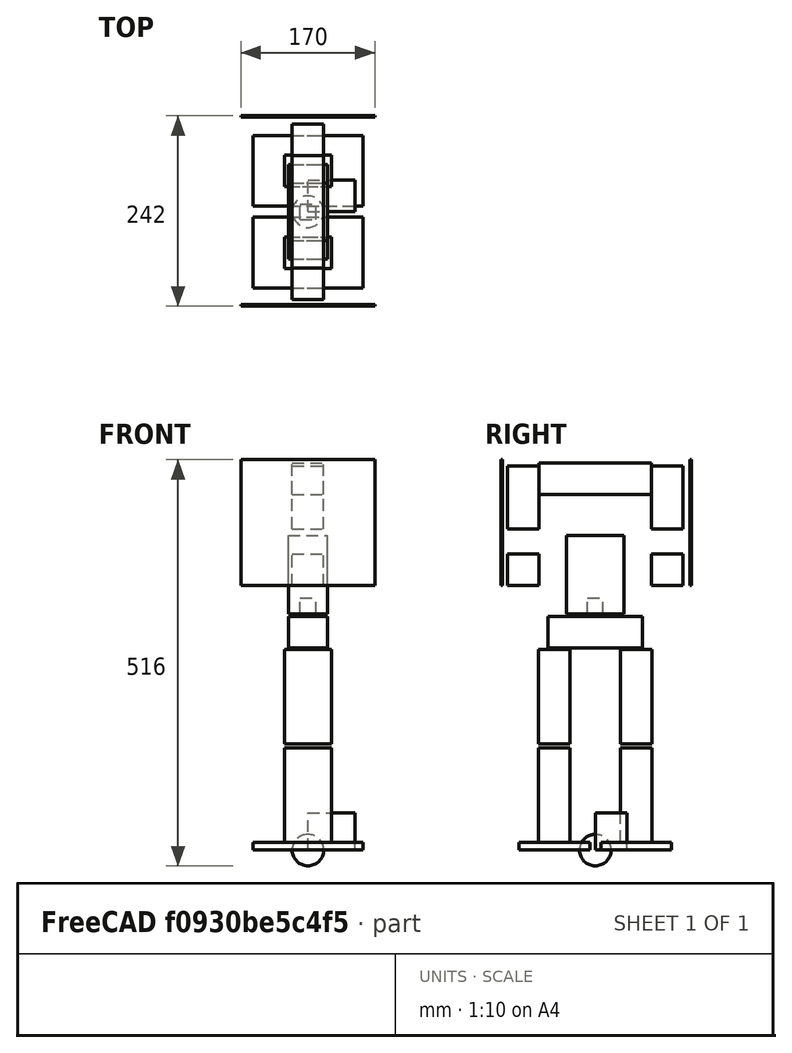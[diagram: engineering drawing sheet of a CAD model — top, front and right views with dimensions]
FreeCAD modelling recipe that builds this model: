
FCSTD DOCUMENT  (FreeCAD 1.1R20260414 (Git shallow))
Label: mj_urdf
License: All rights reserved
LicenseURL: https://en.wikipedia.org/wiki/All_rights_reserved
objects: App::FeaturePython×47, App::Link×43, App::Point×21, App::Part×21, Part::Box×18, Part::Sphere×4, App::DocumentObjectGroup×2, App::DocumentObjectGroupPython×1
note: 22 computed .brp shape members not serialized (recipe doc carries the construction recipe); baked Part::Feature solids carry a one-line shape summary decoded from their .brp

FEATURE [Part::Box] Box001  label="waist_body001"
  AttacherType = Attacher::AttachEngine3D
  Height = 40
  Length = 50
  Placement = pos=(-25,-60,257) rot=(0,0,1;0rad)
  Width = 120
  expr: .Placement.Base.x = -Length / 2
  expr: .Placement.Base.y = -Width / 2
FEATURE [Part::Box] Box002  label="right_thigh"
  AttacherType = Attacher::AttachEngine3D
  Height = 120
  Length = 60
  Placement = pos=(-30,-72,135) rot=(0,0,1;0rad)
  Width = 40
  expr: .Placement.Base.x = -Length / 2
  expr: .Placement.Base.y = -104 mm / 2 - Width / 2
FEATURE [Part::Box] Box003  label="right_shin"
  AttacherType = Attacher::AttachEngine3D
  Height = 120
  Length = 60
  Placement = pos=(-30,-72,10) rot=(0,0,1;0rad)
  Width = 40
  expr: .Placement.Base.x = -Length / 2
  expr: .Placement.Base.y = -104 mm / 2 - Width / 2
FEATURE [Part::Box] Box004  label="right_sole"
  AttacherType = Attacher::AttachEngine3D
  Height = 10
  Length = 140
  Placement = pos=(-70,-97,0) rot=(0,0,1;0rad)
  Width = 90
  expr: .Placement.Base.x = -Length / 2
  expr: .Placement.Base.y = -104 mm / 2 - Width / 2
FEATURE [Part::Box] Box005  label="left_thigh"
  AttacherType = Attacher::AttachEngine3D
  Height = 120
  Length = 60
  Placement = pos=(-30,32,135) rot=(0,0,1;0rad)
  Width = 40
  expr: .Placement.Base.x = -Length / 2
  expr: .Placement.Base.y = +104 mm / 2 - Width / 2
FEATURE [Part::Box] Box006  label="left_shin"
  AttacherType = Attacher::AttachEngine3D
  Height = 120
  Length = 60
  Placement = pos=(-30,32,10) rot=(0,0,1;0rad)
  Width = 40
  expr: .Placement.Base.x = -Length / 2
  expr: .Placement.Base.y = +104 mm / 2 - Width / 2
FEATURE [Part::Box] Box007  label="left_sole"
  AttacherType = Attacher::AttachEngine3D
  Height = 10
  Length = 140
  Placement = pos=(-70,7,0) rot=(0,0,1;0rad)
  Width = 90
  expr: .Placement.Base.x = -Length / 2
  expr: .Placement.Base.y = +104 mm / 2 - Width / 2
FEATURE [Part::Box] Box008  label="body_sholder"
  AttacherType = Attacher::AttachEngine3D
  Height = 40
  Length = 40
  Placement = pos=(-20,-71.5,452) rot=(0,0,1;0rad)
  Width = 143
  expr: .Placement.Base.x = -Length / 2
  expr: .Placement.Base.y = -Width / 2
FEATURE [Part::Box] Box009  label="right_arm"
  AttacherType = Attacher::AttachEngine3D
  Height = 80
  Length = 40
  Placement = pos=(-20,-111.5,408) rot=(0,0,1;0rad)
  Width = 40
  expr: .Placement.Base.x = -Length / 2
  expr: .Placement.Base.y = -143 mm / 2 - Width
FEATURE [Part::Box] Box010  label="right_wrist"
  AttacherType = Attacher::AttachEngine3D
  Height = 40
  Length = 40
  Placement = pos=(-20,-111.5,336) rot=(0,0,1;0rad)
  Width = 40
  expr: .Placement.Base.x = -Length / 2
  expr: .Placement.Base.y = -143 mm / 2 - Width
FEATURE [Part::Box] Box011  label="right_hand"
  AttacherType = Attacher::AttachEngine3D
  Height = 160
  Length = 170
  Placement = pos=(-85,-120,336) rot=(0,0,1;0rad)
  Width = 2
  expr: .Placement.Base.x = -Length / 2
FEATURE [Part::Box] Box012  label="left_arm"
  AttacherType = Attacher::AttachEngine3D
  Height = 80
  Length = 40
  Placement = pos=(-20,71.5,408) rot=(0,0,1;0rad)
  Width = 40
  expr: .Placement.Base.x = -Length / 2
  expr: .Placement.Base.y = +143 mm / 2
FEATURE [Part::Box] Box014  label="left_hand"
  AttacherType = Attacher::AttachEngine3D
  Height = 160
  Length = 170
  Placement = pos=(-85,120,336) rot=(0,0,1;0rad)
  Width = 2
  expr: .Placement.Base.x = -Length / 2
FEATURE [Part::Box] Box  label="body_parts"
  AttacherType = Attacher::AttachEngine3D
  Height = 100
  Length = 50
  Placement = pos=(-25,-36.5,300) rot=(0,0,1;0rad)
  Width = 73
  expr: .Placement.Base.x = -Length / 2
  expr: .Placement.Base.y = -Width / 2
FEATURE [Part::Box] Box013  label="left_wrist"
  AttacherType = Attacher::AttachEngine3D
  Height = 40
  Length = 40
  Placement = pos=(-20,71.5,336) rot=(0,0,1;0rad)
  Width = 40
  expr: .Placement.Base.x = -Length / 2
  expr: .Placement.Base.y = +143 mm / 2
FEATURE [App::Point] Origin001
  Role = Origin
FEATURE [App::Link] waist001  label="waist002"
  LinkedObject = -> Box001
FEATURE [App::Part] waist  label="waist001"
  Group = -> [waist001]
  Origin = -> Origin
FEATURE [App::Link] real_l_waist001_
  LinkPlacement = pos=(-25,-60,362) rot=(0,0,1;0rad)
  LinkedObject = -> waist
  Placement = pos=(-25,-60,362) rot=(0,0,1;0rad)
FEATURE [App::FeaturePython] l_waist001  label="waist"  # WARN: FeaturePython — macro-defined, semantics opaque (R4)
  CalculateInertiaBasedOnMass = false
  Group = -> [real_l_waist001_]
  Ixx = 0
  Ixy = 0
  Ixz = 0
  Iyy = 0
  Iyz = 0
  Izz = 0
  Mass = 0
  MaterialNotCalculate = false
  MountedPlacement = pos=(-25,-60,362) rot=(0,0,1;0rad)
  Placement = pos=(-25,-60,362) rot=(0,0,1;0rad)
  Real = -> [waist]
  Visual = -> [waist]
  _Type = Cross::Link
  expr: .MountedPlacement.Base.x = -<<waist_body001>>.Length / 2
  expr: .MountedPlacement.Base.y = -<<waist_body001>>.Width / 2
FEATURE [App::Point] Origin003
  Role = Origin
FEATURE [App::Link] body001  label="body002"
  LinkedObject = -> Box
FEATURE [App::Link] real_l_body001_
  LinkPlacement = pos=(-25,-36.5,404.5) rot=(0,0,1;0rad)
  LinkedObject = -> body
  Placement = pos=(-25,-36.5,404.5) rot=(0,0,1;0rad)
FEATURE [App::Link] body_sholder001  label="body_sholder002"
  LinkPlacement = pos=(5,-35,100.5) rot=(0,0,1;0rad)
  LinkedObject = -> Box008
  Placement = pos=(5,-35,100.5) rot=(0,0,1;0rad)
  expr: .Placement.Base.x = -<<body_sholder>>.Length / 2 + <<body_parts>>.Length / 2
  expr: .Placement.Base.y = -<<body_sholder>>.Width / 2 + <<body_parts>>.Width / 2
  expr: .Placement.Base.z = 42.5 mm + 78 mm - <<body_sholder>>.Height / 2
FEATURE [App::Point] Origin007  label="Origin009"
  Role = Origin
FEATURE [App::Link] right_thigh001  label="right_thigh002"
  LinkedObject = -> Box002
FEATURE [App::Part] right_thigh  label="right_thigh001"
  Group = -> [right_thigh001]
  Origin = -> Origin006
FEATURE [App::Link] real_l_right_thigh001_
  LinkPlacement = pos=(-30,-72,217) rot=(0,0,1;0rad)
  LinkedObject = -> right_thigh
  Placement = pos=(-30,-72,217) rot=(0,0,1;0rad)
FEATURE [App::FeaturePython] l_right_thigh001  label="r_thigh"  # WARN: FeaturePython — macro-defined, semantics opaque (R4)
  CalculateInertiaBasedOnMass = false
  Group = -> [real_l_right_thigh001_]
  Ixx = 0
  Ixy = 0
  Ixz = 0
  Iyy = 0
  Iyz = 0
  Izz = 0
  Mass = 0
  MaterialNotCalculate = false
  MountedPlacement = pos=(-110,30,20) rot=(-0.57735,0.57735,-0.57735;2.0944rad)
  Placement = pos=(-30,-72,217) rot=(0,0,1;0rad)
  Real = -> [right_thigh]
  Visual = -> [right_thigh]
  _Type = Cross::Link
  expr: .MountedPlacement.Base.y = <<right_thigh>>.Length / 2
  expr: .MountedPlacement.Base.z = <<right_thigh>>.Width / 2
FEATURE [App::Point] Origin009  label="Origin011"
  Role = Origin
FEATURE [App::Link] right_shin001  label="right_shin002"
  LinkedObject = -> Box003
FEATURE [App::Part] right_shin  label="right_shin001"
  Group = -> [right_shin001]
  Origin = -> Origin008
FEATURE [App::Link] real_l_right_shin001_
  LinkPlacement = pos=(-30,-72,70) rot=(0,0,1;0rad)
  LinkedObject = -> right_shin
  Placement = pos=(-30,-72,70) rot=(0,0,1;0rad)
FEATURE [App::FeaturePython] l_right_shin001  label="r_shin"  # WARN: FeaturePython — macro-defined, semantics opaque (R4)
  CalculateInertiaBasedOnMass = false
  Group = -> [real_l_right_shin001_]
  Ixx = 0
  Ixy = 0
  Ixz = 0
  Iyy = 0
  Iyz = 0
  Izz = 0
  Mass = 0
  MaterialNotCalculate = false
  MountedPlacement = pos=(-110,-30,-20) rot=(0.57735,0.57735,0.57735;2.0944rad)
  Placement = pos=(-30,-72,70) rot=(0,0,1;0rad)
  Real = -> [right_shin]
  Visual = -> [right_shin]
  _Type = Cross::Link
  expr: .MountedPlacement.Base.y = -<<right_shin>>.Length / 2
  expr: .MountedPlacement.Base.z = -<<right_shin>>.Width / 2
FEATURE [App::Point] Origin011  label="Origin014"
  Role = Origin
FEATURE [App::Link] right_sole001  label="right_sole002"
  LinkedObject = -> Box004
FEATURE [App::Part] right_sole  label="right_sole001"
  Group = -> [right_sole001]
  Origin = -> Origin010
FEATURE [App::Link] real_l_right_sole001_
  LinkPlacement = pos=(70,-7,1.42e-14) rot=(0,0,1;3.14159rad)
  LinkedObject = -> right_sole
  Placement = pos=(70,-7,1.42e-14) rot=(0,0,1;3.14159rad)
FEATURE [App::FeaturePython] l_right_sole001  label="r_sole"  # WARN: FeaturePython — macro-defined, semantics opaque (R4)
  CalculateInertiaBasedOnMass = false
  Group = -> [real_l_right_sole001_]
  Ixx = 0
  Ixy = 0
  Ixz = 0
  Iyy = 0
  Iyz = 0
  Izz = 0
  Mass = 0
  MaterialNotCalculate = false
  MountedPlacement = pos=(-45,-45,70) rot=(0,-1,0;4.71239rad)
  Placement = pos=(70,-7,1.42e-14) rot=(0,0,1;3.14159rad)
  Real = -> [right_sole]
  Visual = -> [right_sole]
  _Type = Cross::Link
  expr: .MountedPlacement.Base.x = -<<right_sole>>.Height - 35 mm
  expr: .MountedPlacement.Base.y = -<<right_sole>>.Width / 2
  expr: .MountedPlacement.Base.z = <<right_sole>>.Length / 2
FEATURE [App::Point] Origin013  label="Origin017"
  Role = Origin
FEATURE [App::Link] left_thigh001  label="left_thigh002"
  LinkedObject = -> Box005
FEATURE [App::Part] left_thigh  label="left_thigh001"
  Group = -> [left_thigh001]
  Origin = -> Origin012
FEATURE [App::Link] real_l_left_thigh001_
  LinkPlacement = pos=(-30,32,217) rot=(0,0,1;0rad)
  LinkedObject = -> left_thigh
  Placement = pos=(-30,32,217) rot=(0,0,1;0rad)
FEATURE [App::FeaturePython] l_left_thigh001  label="l_thigh"  # WARN: FeaturePython — macro-defined, semantics opaque (R4)
  CalculateInertiaBasedOnMass = false
  Group = -> [real_l_left_thigh001_]
  Ixx = 0
  Ixy = 0
  Ixz = 0
  Iyy = 0
  Iyz = 0
  Izz = 0
  Mass = 0
  MaterialNotCalculate = false
  MountedPlacement = pos=(-110,30,20) rot=(-0.57735,0.57735,-0.57735;2.0944rad)
  Placement = pos=(-30,32,217) rot=(0,0,1;0rad)
  Real = -> [left_thigh]
  Visual = -> [left_thigh]
  _Type = Cross::Link
  expr: .MountedPlacement.Base.x = -110 mm
  expr: .MountedPlacement.Base.y = <<left_thigh>>.Length / 2
  expr: .MountedPlacement.Base.z = <<left_thigh>>.Width / 2
FEATURE [App::Point] Origin015  label="Origin020"
  Role = Origin
FEATURE [App::Link] left_shin001  label="left_shin002"
  LinkedObject = -> Box006
FEATURE [App::Part] left_shin  label="left_shin001"
  Group = -> [left_shin001]
  Origin = -> Origin014
FEATURE [App::Link] real_l_left_shin001_
  LinkPlacement = pos=(-30,32,70) rot=(0,0,1;0rad)
  LinkedObject = -> left_shin
  Placement = pos=(-30,32,70) rot=(0,0,1;0rad)
FEATURE [App::FeaturePython] l_left_shin001  label="l_shin"  # WARN: FeaturePython — macro-defined, semantics opaque (R4)
  CalculateInertiaBasedOnMass = false
  Group = -> [real_l_left_shin001_]
  Ixx = 0
  Ixy = 0
  Ixz = 0
  Iyy = 0
  Iyz = 0
  Izz = 0
  Mass = 0
  MaterialNotCalculate = false
  MountedPlacement = pos=(-110,30,20) rot=(0.57735,-0.57735,0.57735;4.18879rad)
  Placement = pos=(-30,32,70) rot=(0,0,1;0rad)
  Real = -> [left_shin]
  Visual = -> [left_shin]
  _Type = Cross::Link
  expr: .MountedPlacement.Base.x = -110 mm
  expr: .MountedPlacement.Base.y = <<left_shin>>.Length / 2
  expr: .MountedPlacement.Base.z = <<left_shin>>.Width / 2
FEATURE [App::Point] Origin017  label="Origin022"
  Role = Origin
FEATURE [App::Link] left_sole001  label="left_sole002"
  LinkedObject = -> Box007
FEATURE [App::Part] left_sole  label="left_sole001"
  Group = -> [left_sole001]
  Origin = -> Origin016
FEATURE [App::Link] real_l_left_sole001_
  LinkPlacement = pos=(-70,7,-7.1e-15) rot=(0,0,1;0rad)
  LinkedObject = -> left_sole
  Placement = pos=(-70,7,-7.1e-15) rot=(0,0,1;0rad)
FEATURE [App::FeaturePython] l_left_sole001  label="l_sole"  # WARN: FeaturePython — macro-defined, semantics opaque (R4)
  CalculateInertiaBasedOnMass = false
  Group = -> [real_l_left_sole001_]
  Ixx = 0
  Ixy = 0
  Ixz = 0
  Iyy = 0
  Iyz = 0
  Izz = 0
  Mass = 0
  MaterialNotCalculate = false
  MountedPlacement = pos=(-45,-45,70) rot=(0,-1,0;4.71239rad)
  Placement = pos=(-70,7,-7.1e-15) rot=(0,0,1;0rad)
  Real = -> [left_sole]
  Visual = -> [left_sole]
  _Type = Cross::Link
  expr: .MountedPlacement.Base.x = -35 mm - 10 mm
  expr: .MountedPlacement.Base.y = -<<left_sole>>.Width / 2
  expr: .MountedPlacement.Base.z = <<left_sole>>.Length / 2
FEATURE [App::FeaturePython] l_right_sholder001  label="r_p_sholder"  # WARN: FeaturePython — macro-defined, semantics opaque (R4)
  CalculateInertiaBasedOnMass = false
  Ixx = 0
  Ixy = 0
  Ixz = 0
  Iyy = 0
  Iyz = 0
  Izz = 0
  Mass = 0
  MaterialNotCalculate = false
  MountedPlacement = pos=(0,0,0) rot=(1,0,0;1.5708rad)
  Placement = pos=(0,-71.5,525) rot=(1,0,0;3.14159rad)
  _Type = Cross::Link
FEATURE [App::Point] Origin021  label="Origin028"
  Role = Origin
FEATURE [App::Link] right_wrist001  label="right_wrist002"
  LinkedObject = -> Box010
FEATURE [App::Part] right_wrist  label="right_wrist001"
  Group = -> [right_wrist001]
  Origin = -> Origin020
FEATURE [App::Link] real_l_right_wrist001_
  LinkPlacement = pos=(-20,-111.5,402) rot=(0,0,1;0rad)
  LinkedObject = -> right_wrist
  Placement = pos=(-20,-111.5,402) rot=(0,0,1;0rad)
FEATURE [App::FeaturePython] l_right_wrist001  label="r_r_wrist"  # WARN: FeaturePython — macro-defined, semantics opaque (R4)
  CalculateInertiaBasedOnMass = false
  Group = -> [real_l_right_wrist001_]
  Ixx = 0
  Ixy = 0
  Ixz = 0
  Iyy = 0
  Iyz = 0
  Izz = 0
  Mass = 0
  MaterialNotCalculate = false
  MountedPlacement = pos=(20,20,-20) rot=(-0.57735,0.57735,-0.57735;4.18879rad)
  Placement = pos=(-20,-111.5,402) rot=(0,0,1;0rad)
  Real = -> [right_wrist]
  Visual = -> [right_wrist]
  _Type = Cross::Link
  expr: .MountedPlacement.Base.x = <<right_arm>>.Width / 2
  expr: .MountedPlacement.Base.y = <<right_wrist>>.Height / 2
  expr: .MountedPlacement.Base.z = -<<right_wrist>>.Length / 2
FEATURE [App::Point] Origin023  label="Origin031"
  Role = Origin
FEATURE [App::Link] right_hand001  label="right_hand002"
  LinkedObject = -> Box011
FEATURE [App::Part] right_hand  label="right_hand001"
  Group = -> [right_hand001]
  Origin = -> Origin022
FEATURE [App::Link] real_l_right_hand001_
  LinkPlacement = pos=(-85,-114.5,402) rot=(0.707107,0,0.707107;3.14159rad)
  LinkedObject = -> right_hand
  Placement = pos=(-85,-114.5,402) rot=(0.707107,0,0.707107;3.14159rad)
FEATURE [App::FeaturePython] l_right_hand001  label="r_hand"  # WARN: FeaturePython — macro-defined, semantics opaque (R4)
  CalculateInertiaBasedOnMass = false
  Group = -> [real_l_right_hand001_]
  Ixx = 0
  Ixy = 0
  Ixz = 0
  Iyy = 0
  Iyz = 0
  Izz = 0
  Mass = 0
  MaterialNotCalculate = false
  MountedPlacement = pos=(20,-85,3) rot=(0,0.707107,0.707107;3.14159rad)
  Placement = pos=(-85,-114.5,402) rot=(0.707107,0,0.707107;3.14159rad)
  Real = -> [right_hand]
  Visual = -> [right_hand]
  _Type = Cross::Link
  expr: .MountedPlacement.Base.x = <<right_wrist>>.Height / 2
  expr: .MountedPlacement.Base.y = -<<right_hand>>.Length / 2
FEATURE [App::Point] Origin025  label="Origin033"
  Role = Origin
FEATURE [App::Link] left_sholder001  label="left_sholder002"
  LinkedObject = -> Box012
FEATURE [App::Part] left_sholder  label="left_sholder001"
  Group = -> [left_sholder001]
  Origin = -> Origin024
FEATURE [App::FeaturePython] l_left_sholder001  label="l_p_sholder"  # WARN: FeaturePython — macro-defined, semantics opaque (R4)
  CalculateInertiaBasedOnMass = false
  Ixx = 0
  Ixy = 0
  Ixz = 0
  Iyy = 0
  Iyz = 0
  Izz = 0
  Mass = 0
  MaterialNotCalculate = false
  Placement = pos=(0,71.5,525) rot=(1,0,0;1.5708rad)
  _Type = Cross::Link
FEATURE [App::Point] Origin027  label="Origin036"
  Role = Origin
FEATURE [App::Link] left_wrist001  label="left_wrist002"
  LinkedObject = -> Box013
FEATURE [App::Part] left_wrist  label="left_wrist001"
  Group = -> [left_wrist001]
  Origin = -> Origin026
FEATURE [App::Link] real_l_left_wrist001_
  LinkPlacement = pos=(-20,71.5,402) rot=(0,0,1;0rad)
  LinkedObject = -> left_wrist
  Placement = pos=(-20,71.5,402) rot=(0,0,1;0rad)
FEATURE [App::FeaturePython] l_left_wrist001  label="l_r_wrist"  # WARN: FeaturePython — macro-defined, semantics opaque (R4)
  CalculateInertiaBasedOnMass = false
  Group = -> [real_l_left_wrist001_]
  Ixx = 0
  Ixy = 0
  Ixz = 0
  Iyy = 0
  Iyz = 0
  Izz = 0
  Mass = 0
  MaterialNotCalculate = false
  MountedPlacement = pos=(-20,20,20) rot=(-0.57735,-0.57735,0.57735;4.18879rad)
  Placement = pos=(-20,71.5,402) rot=(0,0,1;0rad)
  Real = -> [left_wrist]
  Visual = -> [left_wrist]
  _Type = Cross::Link
  expr: .MountedPlacement.Base.x = -<<left_wrist>>.Width / 2
  expr: .MountedPlacement.Base.y = <<left_wrist>>.Height / 2
  expr: .MountedPlacement.Base.z = <<left_wrist>>.Length / 2
FEATURE [App::Point] Origin029  label="Origin039"
  Role = Origin
FEATURE [App::Link] left_hand001  label="left_hand002"
  LinkedObject = -> Box014
FEATURE [App::Part] left_hand  label="left_hand001"
  Group = -> [left_hand001]
  Origin = -> Origin028
FEATURE [App::Link] real_l_left_hand001_
  LinkPlacement = pos=(85,114.5,402) rot=(0,-1,0;1.5708rad)
  LinkedObject = -> left_hand
  Placement = pos=(85,114.5,402) rot=(0,-1,0;1.5708rad)
FEATURE [App::FeaturePython] l_left_hand001  label="l_hand"  # WARN: FeaturePython — macro-defined, semantics opaque (R4)
  CalculateInertiaBasedOnMass = false
  Group = -> [real_l_left_hand001_]
  Ixx = 0
  Ixy = 0
  Ixz = 0
  Iyy = 0
  Iyz = 0
  Izz = 0
  Mass = 0
  MaterialNotCalculate = false
  MountedPlacement = pos=(85,20,3) rot=(-0.57735,0.57735,0.57735;4.18879rad)
  Placement = pos=(85,114.5,402) rot=(0,-1,0;1.5708rad)
  Real = -> [left_hand]
  Visual = -> [left_hand]
  _Type = Cross::Link
  expr: .MountedPlacement.Base.x = <<left_hand>>.Length / 2
  expr: .MountedPlacement.Base.y = <<left_wrist>>.Height / 2
FEATURE [App::FeaturePython] l_waist001__to__l_body001  label="waist_joint"  # WARN: FeaturePython — macro-defined, semantics opaque (R4)
  Child = 1
  Effort = 0
  JoinRotationDirection = 0
  JointSpecific = 0
  LowerLimit = -90
  Mimic = false
  Multiplier = -1
  Origin = pos=(0,0,404.5) rot=(0,0,1;0rad)
  Parent = 1
  ParentOldTmp = not_a_FreeCAD_object_4NUJw9
  Placement = pos=(0,0,404.5) rot=(0,0,1;0rad)
  Position = 0
  Type = 2
  UpperLimit = 90
  Velocity = 0
  _Type = Cross::Joint
  expr: .Origin.Base.z = <<waist>>.Placement.Base.z + 42.5 mm
FEATURE [App::FeaturePython] l_right_wrist001__to__l_right_hand001  label="r_hand_joint"  # WARN: FeaturePython — macro-defined, semantics opaque (R4)
  Child = 1
  ChildOldTmp = not_a_FreeCAD_object_n2sEOj
  Effort = 0
  JoinRotationDirection = 0
  JointSpecific = 0
  LowerLimit = -90
  Mimic = false
  Multiplier = 1
  Origin = pos=(20,0,0) rot=(0.57735,0.57735,0.57735;2.0944rad)
  Parent = 18
  Placement = pos=(0,-111.5,422) rot=(0.57735,0.57735,-0.57735;2.0944rad)
  Position = 0
  Type = 2
  UpperLimit = 90
  Velocity = 0
  _Type = Cross::Joint
FEATURE [Part::Sphere] Sphere  label="right_hip"
  Angle1 = -90
  Angle2 = 90
  Angle3 = 360
  AttacherType = Attacher::AttachEngine3D
  Radius = 20
FEATURE [App::Point] Origin031  label="Origin041"
  Role = Origin
FEATURE [App::Link] right_hip001  label="right_hip002"
  LinkedObject = -> Sphere
FEATURE [App::Part] right_hip  label="right_hip001"
  Group = -> [right_hip001]
  Origin = -> Origin030
FEATURE [App::Link] real_l_right_hip001_
  LinkPlacement = pos=(0,-52,362) rot=(0,0,1;0rad)
  LinkedObject = -> right_hip
  Placement = pos=(0,-52,362) rot=(0,0,1;0rad)
FEATURE [App::FeaturePython] l_right_hip001  label="r_hip"  # WARN: FeaturePython — macro-defined, semantics opaque (R4)
  CalculateInertiaBasedOnMass = false
  Group = -> [real_l_right_hip001_]
  Ixx = 0
  Ixy = 0
  Ixz = 0
  Iyy = 0
  Iyz = 0
  Izz = 0
  Mass = 0
  MaterialNotCalculate = false
  MountedPlacement = pos=(0,0,0) rot=(0,-1,0;4.71239rad)
  Placement = pos=(0,-52,362) rot=(0,0,1;0rad)
  Real = -> [right_hip]
  Visual = -> [right_hip]
  _Type = Cross::Link
FEATURE [App::FeaturePython] l_waist001__to__l_right_hip001  label="r_hip_joint"  # WARN: FeaturePython — macro-defined, semantics opaque (R4)
  Child = 1
  Effort = 0
  JoinRotationDirection = 0
  JointSpecific = 0
  LowerLimit = -90
  Mimic = false
  Multiplier = 1
  Origin = pos=(0,-52,362) rot=(0,-1,0;1.5708rad)
  Parent = 1
  ParentOldTmp = not_a_FreeCAD_object_4VV3ZL
  Placement = pos=(0,-52,362) rot=(0,-1,0;1.5708rad)
  Position = 0
  Type = 2
  UpperLimit = 90
  Velocity = 0
  _Type = Cross::Joint
  expr: .Origin.Base.y = -104 / 2
  expr: .Origin.Base.z = <<waist>>.Placement.Base.z
FEATURE [App::FeaturePython] l_right_hip001__to__l_right_thigh001  label="r_thigh_top_joint"  # WARN: FeaturePython — macro-defined, semantics opaque (R4)
  Child = 1
  Effort = 0
  JoinRotationDirection = 0
  JointSpecific = 0
  LowerLimit = -90
  Mimic = false
  Multiplier = -1
  Origin = pos=(-35,0,0) rot=(1,0,0;1.5708rad)
  Parent = 3
  Placement = pos=(0,-52,327) rot=(0.57735,-0.57735,0.57735;2.0944rad)
  Position = 0
  Type = 2
  UpperLimit = 90
  Velocity = 0
  _Type = Cross::Joint
  expr: .Origin.Base.x = -35 mm
FEATURE [Part::Box] Box015  label="right_knee"
  AttacherType = Attacher::AttachEngine3D
  Height = 47
  Length = 60
  Width = 40
FEATURE [App::Point] Origin033  label="Origin044"
  Role = Origin
FEATURE [App::Link] right_knee001  label="right_knee002"
  LinkedObject = -> Box015
FEATURE [App::Part] right_knee  label="right_knee001"
  Group = -> [right_knee001]
  Origin = -> Origin032
FEATURE [App::Link] real_l_right_knee001_
  LinkPlacement = pos=(-30,-72,180) rot=(0,0,1;0rad)
  LinkedObject = -> right_knee
  Placement = pos=(-30,-72,180) rot=(0,0,1;0rad)
FEATURE [App::FeaturePython] l_right_knee001  label="r_knee"  # WARN: FeaturePython — macro-defined, semantics opaque (R4)
  CalculateInertiaBasedOnMass = false
  Group = -> [real_l_right_knee001_]
  Ixx = 0
  Ixy = 0
  Ixz = 0
  Iyy = 0
  Iyz = 0
  Izz = 0
  Mass = 0
  MaterialNotCalculate = false
  MountedPlacement = pos=(-47,30,20) rot=(0.57735,-0.57735,0.57735;4.18879rad)
  Placement = pos=(-30,-72,180) rot=(0,0,1;0rad)
  Real = -> [right_knee]
  Visual = -> [right_knee]
  _Type = Cross::Link
  expr: .MountedPlacement.Base.x = -<<right_knee>>.Height
  expr: .MountedPlacement.Base.y = <<right_knee>>.Length / 2
  expr: .MountedPlacement.Base.z = <<right_knee>>.Width / 2 mm
FEATURE [App::FeaturePython] l_right_thigh001__to__l_right_knee001  label="r_thigh_bottom_joint"  # WARN: FeaturePython — macro-defined, semantics opaque (R4)
  Child = 1
  Effort = 0
  JoinRotationDirection = 0
  JointSpecific = 0
  LowerLimit = -90
  Mimic = true
  MimickedJoint = -> l_right_hip001__to__l_right_thigh001
  Multiplier = -1
  Origin = pos=(-100,0,0) rot=(0,1,0;0rad)
  Parent = 4
  Placement = pos=(0,-52,227) rot=(0.57735,-0.57735,0.57735;2.0944rad)
  Position = 0
  Type = 2
  UpperLimit = 90
  Velocity = 0
  _Type = Cross::Joint
  expr: .Origin.Base.x = -100 mm
FEATURE [App::FeaturePython] l_right_knee001__to__l_right_shin001  label="r_shin_top_joint"  # WARN: FeaturePython — macro-defined, semantics opaque (R4)
  Child = 1
  Effort = 0
  JoinRotationDirection = 0
  JointSpecific = 0
  LowerLimit = -90
  Mimic = false
  Multiplier = 1
  Origin = pos=(-47,0,0) rot=(1,0,0;3.14159rad)
  Parent = 5
  Placement = pos=(0,-52,180) rot=(0.57735,0.57735,0.57735;4.18879rad)
  Position = 0
  Type = 2
  UpperLimit = 90
  Velocity = 0
  _Type = Cross::Joint
  expr: .Origin.Base.x = -47
FEATURE [Part::Sphere] Sphere001  label="right_ankle"
  Angle1 = -90
  Angle2 = 90
  Angle3 = 360
  AttacherType = Attacher::AttachEngine3D
  Radius = 20
FEATURE [App::Point] Origin035  label="Origin047"
  Role = Origin
FEATURE [App::Link] right_ankle001  label="right_ankle002"
  LinkedObject = -> Sphere001
FEATURE [App::Part] right_ankle  label="right_ankle001"
  Group = -> [right_ankle001]
  Origin = -> Origin034
FEATURE [App::Link] real_l_right_ankle001_
  LinkPlacement = pos=(0,-52,45) rot=(0,0,1;0rad)
  LinkedObject = -> right_ankle
  Placement = pos=(0,-52,45) rot=(0,0,1;0rad)
FEATURE [App::FeaturePython] l_right_ankle001  label="r_ankle"  # WARN: FeaturePython — macro-defined, semantics opaque (R4)
  CalculateInertiaBasedOnMass = false
  Group = -> [real_l_right_ankle001_]
  Ixx = 0
  Ixy = 0
  Ixz = 0
  Iyy = 0
  Iyz = 0
  Izz = 0
  Mass = 0
  MaterialNotCalculate = false
  MountedPlacement = pos=(-35,0,0) rot=(-0.57735,-0.57735,-0.57735;4.18879rad)
  Placement = pos=(0,-52,45) rot=(0,0,1;0rad)
  Real = -> [right_ankle]
  Visual = -> [right_ankle]
  _Type = Cross::Link
FEATURE [App::FeaturePython] l_right_shin001__to__l_right_ankle001  label="r_shin_bottom_joint"  # WARN: FeaturePython — macro-defined, semantics opaque (R4)
  Child = 1
  Effort = 0
  JoinRotationDirection = 0
  JointSpecific = 0
  LowerLimit = -90
  Mimic = true
  MimickedJoint = -> l_right_knee001__to__l_right_shin001
  Multiplier = -1
  Origin = pos=(-100,0,0) rot=(0,0,1;0rad)
  Parent = 6
  Placement = pos=(0,-52,80) rot=(0.57735,0.57735,0.57735;4.18879rad)
  Position = 0
  Type = 2
  UpperLimit = 90
  Velocity = 0
  _Type = Cross::Joint
  expr: .Origin.Base.x = -100 mm
FEATURE [App::FeaturePython] l_right_ankle001__to__l_right_sole001  label="r_ankle_joint"  # WARN: FeaturePython — macro-defined, semantics opaque (R4)
  Child = 1
  Effort = 0
  JoinRotationDirection = 0
  JointSpecific = 0
  LowerLimit = -90
  Mimic = false
  Multiplier = 1
  Origin = pos=(-35,0,0) rot=(1,0,0;4.71239rad)
  Parent = 7
  Placement = pos=(0,-52,45) rot=(-0.707107,0,-0.707107;3.14159rad)
  Position = 0
  Type = 2
  UpperLimit = 90
  Velocity = 0
  _Type = Cross::Joint
FEATURE [Part::Sphere] Sphere002  label="left_hip"
  Angle1 = -90
  Angle2 = 90
  Angle3 = 360
  AttacherType = Attacher::AttachEngine3D
  Radius = 20
FEATURE [Part::Sphere] Sphere003  label="left_ankle"
  Angle1 = -90
  Angle2 = 90
  Angle3 = 360
  AttacherType = Attacher::AttachEngine3D
  Radius = 20
FEATURE [Part::Box] Box016  label="left_knee"
  AttacherType = Attacher::AttachEngine3D
  Height = 47
  Length = 60
  Width = 40
FEATURE [App::Point] Origin037  label="Origin050"
  Role = Origin
FEATURE [App::Link] left_ankle001  label="left_ankle002"
  LinkedObject = -> Sphere003
FEATURE [App::Part] left_ankle  label="left_ankle001"
  Group = -> [left_ankle001]
  Origin = -> Origin036
FEATURE [App::Link] real_l_left_ankle001_
  LinkPlacement = pos=(0,52,45) rot=(0.57735,-0.57735,0.57735;2.0944rad)
  LinkedObject = -> left_ankle
  Placement = pos=(0,52,45) rot=(0.57735,-0.57735,0.57735;2.0944rad)
FEATURE [App::FeaturePython] l_left_ankle001  label="l_ankle"  # WARN: FeaturePython — macro-defined, semantics opaque (R4)
  CalculateInertiaBasedOnMass = false
  Group = -> [real_l_left_ankle001_]
  Ixx = 0
  Ixy = 0
  Ixz = 0
  Iyy = 0
  Iyz = 0
  Izz = 0
  Mass = 0
  MaterialNotCalculate = false
  MountedPlacement = pos=(-35,0,0) rot=(0,0,1;0rad)
  Placement = pos=(0,52,45) rot=(0.57735,-0.57735,0.57735;2.0944rad)
  Real = -> [left_ankle]
  Visual = -> [left_ankle]
  _Type = Cross::Link
FEATURE [App::Point] Origin039  label="Origin052"
  Role = Origin
FEATURE [App::Link] left_hip001  label="left_hip002"
  LinkedObject = -> Sphere002
FEATURE [App::Part] left_hip  label="left_hip001"
  Group = -> [left_hip001]
  Origin = -> Origin038
FEATURE [App::Link] real_l_left_hip001_
  LinkPlacement = pos=(0,52,362) rot=(0.707107,0,0.707107;3.14159rad)
  LinkedObject = -> left_hip
  Placement = pos=(0,52,362) rot=(0.707107,0,0.707107;3.14159rad)
FEATURE [App::FeaturePython] l_left_hip001  label="l_hip"  # WARN: FeaturePython — macro-defined, semantics opaque (R4)
  CalculateInertiaBasedOnMass = false
  Group = -> [real_l_left_hip001_]
  Ixx = 0
  Ixy = 0
  Ixz = 0
  Iyy = 0
  Iyz = 0
  Izz = 0
  Mass = 0
  MaterialNotCalculate = false
  Placement = pos=(0,52,362) rot=(0.707107,0,0.707107;3.14159rad)
  Real = -> [left_hip]
  Visual = -> [left_hip]
  _Type = Cross::Link
FEATURE [App::Point] Origin041  label="Origin055"
  Role = Origin
FEATURE [App::Link] left_knee001  label="left_knee002"
  LinkedObject = -> Box016
FEATURE [App::Part] left_knee  label="left_knee001"
  Group = -> [left_knee001]
  Origin = -> Origin040
FEATURE [App::Link] real_l_left_knee001_
  LinkPlacement = pos=(-30,32,180) rot=(0,0,1;0rad)
  LinkedObject = -> left_knee
  Placement = pos=(-30,32,180) rot=(0,0,1;0rad)
FEATURE [App::FeaturePython] l_left_knee001  label="l_knee"  # WARN: FeaturePython — macro-defined, semantics opaque (R4)
  CalculateInertiaBasedOnMass = false
  Group = -> [real_l_left_knee001_]
  Ixx = 0
  Ixy = 0
  Ixz = 0
  Iyy = 0
  Iyz = 0
  Izz = 0
  Mass = 0
  MaterialNotCalculate = false
  MountedPlacement = pos=(-47,30,20) rot=(-0.57735,0.57735,-0.57735;2.0944rad)
  Placement = pos=(-30,32,180) rot=(0,0,1;0rad)
  Real = -> [left_knee]
  Visual = -> [left_knee]
  _Type = Cross::Link
  expr: .MountedPlacement.Base.x = -47
  expr: .MountedPlacement.Base.y = <<left_knee>>.Length / 2
  expr: .MountedPlacement.Base.z = <<left_knee>>.Width / 2
FEATURE [App::FeaturePython] l_left_hip001__to__l_left_thigh001  label="l_thigh_top_joint"  # WARN: FeaturePython — macro-defined, semantics opaque (R4)
  Child = 1
  Effort = 0
  JoinRotationDirection = 0
  JointSpecific = 0
  LowerLimit = -90
  Mimic = false
  Multiplier = 1
  Origin = pos=(-35,0,0) rot=(-1,0,0;1.5708rad)
  Parent = 9
  Placement = pos=(0,52,327) rot=(0.57735,-0.57735,0.57735;2.0944rad)
  Position = 0
  Type = 2
  UpperLimit = 90
  Velocity = 0
  _Type = Cross::Joint
FEATURE [App::FeaturePython] l_left_thigh001__to__l_left_knee001  label="l_thigh_bottom_joint"  # WARN: FeaturePython — macro-defined, semantics opaque (R4)
  Child = 1
  Effort = 0
  JoinRotationDirection = 0
  JointSpecific = 0
  LowerLimit = -90
  Mimic = true
  MimickedJoint = -> l_left_hip001__to__l_left_thigh001
  Multiplier = -1
  Origin = pos=(-100,0,0) rot=(0,0,1;0rad)
  Parent = 10
  Placement = pos=(0,52,227) rot=(0.57735,-0.57735,0.57735;2.0944rad)
  Position = 0
  Type = 2
  UpperLimit = 90
  Velocity = 0
  _Type = Cross::Joint
FEATURE [App::FeaturePython] l_left_knee001__to__l_left_shin001  label="l_shin_top_joint"  # WARN: FeaturePython — macro-defined, semantics opaque (R4)
  Child = 1
  Effort = 0
  JoinRotationDirection = 0
  JointSpecific = 0
  LowerLimit = -90
  Mimic = false
  Multiplier = 1
  Origin = pos=(-47,0,0) rot=(0,0,1;0rad)
  Parent = 11
  Placement = pos=(0,52,180) rot=(0.57735,-0.57735,0.57735;2.0944rad)
  Position = 0
  Type = 2
  UpperLimit = 90
  Velocity = 0
  _Type = Cross::Joint
FEATURE [App::FeaturePython] l_left_shin001__to__l_left_ankle001  label="l_shin_bottom_joint"  # WARN: FeaturePython — macro-defined, semantics opaque (R4)
  Child = 1
  Effort = 0
  JoinRotationDirection = 0
  JointSpecific = 0
  LowerLimit = -90
  Mimic = true
  MimickedJoint = -> l_left_knee001__to__l_left_shin001
  Multiplier = -1
  Origin = pos=(-100,0,0) rot=(0,0,1;0rad)
  Parent = 12
  Placement = pos=(0,52,80) rot=(0.57735,-0.57735,0.57735;2.0944rad)
  Position = 0
  Type = 2
  UpperLimit = 90
  Velocity = 0
  _Type = Cross::Joint
FEATURE [App::FeaturePython] l_left_ankle001__to__l_left_sole001  label="l_ankle_joint"  # WARN: FeaturePython — macro-defined, semantics opaque (R4)
  Child = 1
  Effort = 0
  JoinRotationDirection = 0
  JointSpecific = 0
  LowerLimit = -90
  Mimic = false
  Multiplier = 1
  Origin = pos=(-35,0,0) rot=(-1,0,0;1.5708rad)
  Parent = 13
  Placement = pos=(0,52,45) rot=(0,-1,0;1.5708rad)
  Position = 0
  Type = 2
  UpperLimit = 90
  Velocity = 0
  _Type = Cross::Joint
FEATURE [App::FeaturePython] l_body001__to__l_right_sholder001  label="r_p_sholder_joint"  # WARN: FeaturePython — macro-defined, semantics opaque (R4)
  Child = 1
  ChildOldTmp = not_a_FreeCAD_object_oeAF9K
  Effort = 0
  JoinRotationDirection = 0
  JointSpecific = 0
  LowerLimit = -90
  Mimic = false
  Multiplier = 1
  Origin = pos=(0,-71.5,120.5) rot=(1,0,0;1.5708rad)
  Parent = 2
  Placement = pos=(0,-71.5,525) rot=(1,0,0;1.5708rad)
  Position = 0
  Type = 2
  UpperLimit = 90
  Velocity = 0
  _Type = Cross::Joint
  expr: .Origin.Base.y = -<<body_sholder>>.Width / 2
  expr: .Origin.Base.z = 42.5 mm + 78 mm
FEATURE [App::Point] Origin043  label="Origin058"
  Role = Origin
FEATURE [App::Link] right_arm001  label="right_arm002"
  LinkedObject = -> Box009
FEATURE [App::Part] right_arm  label="right_arm001"
  Group = -> [right_arm001]
  Origin = -> Origin042
FEATURE [App::Link] real_l_right_arm001_
  LinkPlacement = pos=(-20,-111.5,462.5) rot=(0,0,1;0rad)
  LinkedObject = -> right_arm
  Placement = pos=(-20,-111.5,462.5) rot=(0,0,1;0rad)
FEATURE [App::FeaturePython] l_right_arm001  label="r_r_sholder"  # WARN: FeaturePython — macro-defined, semantics opaque (R4)
  CalculateInertiaBasedOnMass = false
  Group = -> [real_l_right_arm001_]
  Ixx = 0
  Ixy = 0
  Ixz = 0
  Iyy = 0
  Iyz = 0
  Izz = 0
  Mass = 0
  MaterialNotCalculate = false
  MountedPlacement = pos=(20,-62.5,20) rot=(-0.57735,0.57735,0.57735;2.0944rad)
  Placement = pos=(-20,-111.5,462.5) rot=(0,0,1;0rad)
  Real = -> [right_arm]
  Visual = -> [right_arm]
  _Type = Cross::Link
  expr: .MountedPlacement.Base.x = <<right_arm>>.Width / 2
  expr: .MountedPlacement.Base.y = -<<right_arm>>.Height + <<body_sholder>>.Height / 2 - 2.5 mm
  expr: .MountedPlacement.Base.z = <<right_arm>>.Length / 2
FEATURE [App::FeaturePython] l_right_sholder001__to__l_right_arm001  label="r_r_sholder_joint"  # WARN: FeaturePython — macro-defined, semantics opaque (R4)
  Child = 1
  ChildOldTmp = not_a_FreeCAD_object_9fuDFF
  Effort = 0
  JoinRotationDirection = 0
  JointSpecific = 0
  LowerLimit = -90
  Mimic = false
  Multiplier = 1
  Origin = pos=(0,0,20) rot=(0,-1,0;1.5708rad)
  Parent = 15
  ParentOldTmp = not_a_FreeCAD_object_MLccNK
  Placement = pos=(0,-91.5,525) rot=(0.57735,-0.57735,-0.57735;2.0944rad)
  Position = 0
  Type = 2
  UpperLimit = 90
  Velocity = 0
  _Type = Cross::Joint
  expr: .Origin.Base.z = <<right_arm>>.Width / 2
FEATURE [App::FeaturePython] Link  label="r_y_wrist"  # WARN: FeaturePython — macro-defined, semantics opaque (R4)
  CalculateInertiaBasedOnMass = false
  Ixx = 0
  Ixy = 0
  Ixz = 0
  Iyy = 0
  Iyz = 0
  Izz = 0
  Mass = 0
  MaterialNotCalculate = false
  Placement = pos=(0,-91.5,455) rot=(0,0,-1;1.5708rad)
  _Type = Cross::Link
FEATURE [App::FeaturePython] l_right_arm001__to__l_right_wrist_yaw  label="r_y_wrist_joint"  # WARN: FeaturePython — macro-defined, semantics opaque (R4)
  Child = 1
  ChildOldTmp = not_a_FreeCAD_object_SHMXh9
  Effort = 0
  JoinRotationDirection = 0
  JointSpecific = 0
  LowerLimit = -90
  Mimic = false
  Multiplier = 1
  Origin = pos=(0,-70,0) rot=(-1,0,0;1.5708rad)
  Parent = 16
  ParentOldTmp = not_a_FreeCAD_object_VCmshN
  Placement = pos=(0,-91.5,455) rot=(0,0,-1;1.5708rad)
  Position = 0
  Type = 2
  UpperLimit = 90
  Velocity = 0
  _Type = Cross::Joint
  expr: .Origin.Base.y = -70
FEATURE [App::FeaturePython] l_right_wrist_yaw__to__l_right_wrist001  label="r_r_wrist_joint"  # WARN: FeaturePython — macro-defined, semantics opaque (R4)
  Child = 1
  Effort = 0
  JoinRotationDirection = 0
  JointSpecific = 0
  LowerLimit = 0
  Mimic = false
  Multiplier = 1
  Origin = pos=(0,0,-33) rot=(-1,0,0;1.5708rad)
  Parent = 17
  ParentOldTmp = not_a_FreeCAD_object_92NpWE
  Placement = pos=(0,-91.5,422) rot=(-0.57735,0.57735,-0.57735;2.0944rad)
  Position = 0
  Type = 2
  UpperLimit = 180
  Velocity = 0
  _Type = Cross::Joint
FEATURE [App::FeaturePython] l_waist001__to__l_left_hip001  label="l_hip_joint"  # WARN: FeaturePython — macro-defined, semantics opaque (R4)
  Child = 1
  Effort = 0
  JoinRotationDirection = 0
  JointSpecific = 0
  LowerLimit = -90
  Mimic = false
  Multiplier = 1
  Origin = pos=(0,52,362) rot=(0.707107,0,0.707107;3.14159rad)
  Parent = 1
  ParentOldTmp = not_a_FreeCAD_object_E4VMrj
  Placement = pos=(0,52,362) rot=(0.707107,0,0.707107;3.14159rad)
  Position = 0
  Type = 2
  UpperLimit = 90
  Velocity = 0
  _Type = Cross::Joint
FEATURE [App::Point] Origin045  label="Origin061"
  Role = Origin
FEATURE [App::Link] left_arm001  label="left_arm002"
  LinkedObject = -> Box012
FEATURE [App::Part] left_arm  label="left_arm001"
  Group = -> [left_arm001]
  Origin = -> Origin044
FEATURE [App::Link] real_l_left_arm001_
  LinkPlacement = pos=(-20,71.5,462.5) rot=(0,0,1;0rad)
  LinkedObject = -> left_arm
  Placement = pos=(-20,71.5,462.5) rot=(0,0,1;0rad)
FEATURE [App::FeaturePython] l_left_arm001  label="l_r_sholder"  # WARN: FeaturePython — macro-defined, semantics opaque (R4)
  CalculateInertiaBasedOnMass = false
  Group = -> [real_l_left_arm001_]
  Ixx = 0
  Ixy = 0
  Ixz = 0
  Iyy = 0
  Iyz = 0
  Izz = 0
  Mass = 0
  MaterialNotCalculate = false
  MountedPlacement = pos=(-20,-62.5,-20) rot=(0.57735,0.57735,0.57735;4.18879rad)
  Placement = pos=(-20,71.5,462.5) rot=(0,0,1;0rad)
  Real = -> [left_arm]
  Visual = -> [left_arm]
  _Type = Cross::Link
  expr: .MountedPlacement.Base.x = -<<left_arm>>.Width / 2
  expr: .MountedPlacement.Base.y = -<<left_arm>>.Height + <<body_sholder>>.Height / 2 - 2.5 mm
  expr: .MountedPlacement.Base.z = -<<left_arm>>.Length / 2
FEATURE [App::FeaturePython] Link001  label="l_y_wrist"  # WARN: FeaturePython — macro-defined, semantics opaque (R4)
  CalculateInertiaBasedOnMass = false
  Ixx = 0
  Ixy = 0
  Ixz = 0
  Iyy = 0
  Iyz = 0
  Izz = 0
  Mass = 0
  MaterialNotCalculate = false
  Placement = pos=(0,91.5,455) rot=(0.707107,0.707107,0;3.14159rad)
  _Type = Cross::Link
FEATURE [App::FeaturePython] l_left_sholder001__to__l_left_arm001  label="l_r_sholder_joint"  # WARN: FeaturePython — macro-defined, semantics opaque (R4)
  Child = 1
  Effort = 0
  JoinRotationDirection = 0
  JointSpecific = 0
  LowerLimit = -90
  Mimic = false
  Multiplier = 1
  Origin = pos=(0,0,-20) rot=(0,1,0;1.5708rad)
  Parent = 20
  Placement = pos=(0,91.5,525) rot=(0.57735,0.57735,0.57735;2.0944rad)
  Position = 0
  Type = 2
  UpperLimit = 90
  Velocity = 0
  _Type = Cross::Joint
  expr: .Origin.Base.z = -<<left_arm>>.Width / 2
FEATURE [App::FeaturePython] l_left_arm001__to__l_left_wrist_yaw001  label="l_y_wrist_joint"  # WARN: FeaturePython — macro-defined, semantics opaque (R4)
  Child = 1
  ChildOldTmp = not_a_FreeCAD_object_EKxtcE
  Effort = 0
  JoinRotationDirection = 0
  JointSpecific = 0
  LowerLimit = -90
  Mimic = false
  Multiplier = 1
  Origin = pos=(0,-70,0) rot=(1,0,0;1.5708rad)
  Parent = 21
  Placement = pos=(0,91.5,455) rot=(0.707107,0.707107,0;3.14159rad)
  Position = 0
  Type = 2
  UpperLimit = 90
  Velocity = 0
  _Type = Cross::Joint
FEATURE [App::FeaturePython] l_left_wrist_yaw001__to__l_left_wrist001  label="l_r_wrist_joint"  # WARN: FeaturePython — macro-defined, semantics opaque (R4)
  Child = 1
  Effort = 0
  JoinRotationDirection = 0
  JointSpecific = 0
  LowerLimit = 0
  Mimic = false
  Multiplier = 1
  Origin = pos=(0,0,33) rot=(1,0,0;1.5708rad)
  Parent = 22
  ParentOldTmp = not_a_FreeCAD_object_miIBEU
  Placement = pos=(0,91.5,422) rot=(0.57735,0.57735,-0.57735;4.18879rad)
  Position = 0
  Type = 2
  UpperLimit = 180
  Velocity = 0
  _Type = Cross::Joint
FEATURE [App::FeaturePython] l_left_wrist001__to__l_left_hand001  label="l_hand_joint"  # WARN: FeaturePython — macro-defined, semantics opaque (R4)
  Child = 1
  Effort = 0
  JoinRotationDirection = 0
  JointSpecific = 0
  LowerLimit = -90
  Mimic = false
  Multiplier = 1
  Origin = pos=(20,0,0) rot=(0,1,0;1.5708rad)
  Parent = 23
  Placement = pos=(0,111.5,422) rot=(1,0,0;4.71239rad)
  Position = 0
  Type = 2
  UpperLimit = 90
  Velocity = 0
  _Type = Cross::Joint
FEATURE [App::FeaturePython] l_body001__to__l_left_sholder001  label="l_p_sholder_joint"  # WARN: FeaturePython — macro-defined, semantics opaque (R4)
  Child = 1
  Effort = 0
  JoinRotationDirection = 0
  JointSpecific = 0
  LowerLimit = -90
  Mimic = false
  Multiplier = 1
  Origin = pos=(0,71.5,120.5) rot=(1,0,0;1.5708rad)
  Parent = 2
  Placement = pos=(0,71.5,525) rot=(1,0,0;1.5708rad)
  Position = 0
  Type = 2
  UpperLimit = 90
  Velocity = 0
  _Type = Cross::Joint
  expr: .Origin.Base.y = <<body_sholder>>.Width / 2
  expr: .Origin.Base.z = 42.5 mm + 78 mm
FEATURE [Part::Box] Box017  label="body_head"
  AttacherType = Attacher::AttachEngine3D
  Height = 20
  Length = 20
  Placement = pos=(-10,-10,300) rot=(0,0,1;0rad)
  Width = 20
  expr: .Placement.Base.x = -Length / 2
  expr: .Placement.Base.y = -Width / 2
FEATURE [App::DocumentObjectGroup] robot_parts_origins
  Group = -> [Box001,Box,Box008,Box017,Box002,Box003,Box004,Box005,Box006,Box007,Box009,Box010,Box011,Box013,Box014,Sphere,Box015,Sphere001,Sphere003,Sphere002,Box016,Box012]
FEATURE [App::Link] Link002  label="body_head001"
  LinkPlacement = pos=(25,25,141) rot=(0,0,1;0rad)
  LinkedObject = -> Box017
  Placement = pos=(25,25,141) rot=(0,0,1;0rad)
FEATURE [App::Part] body  label="body001"
  Group = -> [body001,body_sholder001,Link002]
  Origin = -> Origin002
FEATURE [App::DocumentObjectGroup] robot_parts
  Group = -> [waist,body,right_thigh,right_shin,right_sole,left_thigh,left_shin,left_sole,right_arm,right_wrist,right_hand,left_sholder,left_wrist,left_hand,right_hip,right_knee,right_ankle,left_ankle,left_hip,left_knee,left_arm]
FEATURE [App::FeaturePython] l_body001  label="body"  # WARN: FeaturePython — macro-defined, semantics opaque (R4)
  CalculateInertiaBasedOnMass = false
  Group = -> [real_l_body001_]
  Ixx = 0
  Ixy = 0
  Ixz = 0
  Iyy = 0
  Iyz = 0
  Izz = 0
  Mass = 0
  MaterialNotCalculate = false
  MountedPlacement = pos=(-25,-36.5,0) rot=(0,0,1;0rad)
  Placement = pos=(-25,-36.5,404.5) rot=(0,0,1;0rad)
  Real = -> [body]
  Visual = -> [body]
  _Type = Cross::Link
  expr: .MountedPlacement.Base.x = -<<body_parts>>.Length / 2
  expr: .MountedPlacement.Base.y = -<<body_parts>>.Width / 2
FEATURE [App::DocumentObjectGroupPython] Robot  # scripted group (container) (typed FeaturePython)
  GenerateCodeForRosVersion = 0
  Group = -> [l_waist001,l_body001,l_right_hip001,l_right_thigh001,l_right_knee001,l_right_shin001,l_right_ankle001,l_right_sole001,l_left_hip001,l_left_thigh001,l_left_knee001,l_left_shin001,l_left_ankle001,l_left_sole001,l_right_sholder001,l_right_arm001,Link,l_right_wrist001,l_right_hand001,l_left_sholder001,l_left_arm001,Link001,l_left_wrist001,l_left_hand001,l_waist001__to__l_body001,+22 more]
  Mass = 0
  RobotType = 0
  _Type = Cross::Robot
  l_ankle_joint_deg = 0
  l_hand_joint_deg = 0
  l_hip_joint_deg = 0
  l_p_sholder_joint_deg = 0
  l_r_sholder_joint_deg = 0
  l_r_wrist_joint_deg = 0
  l_shin_top_joint_deg = 0
  l_thigh_top_joint_deg = 0
  l_y_wrist_joint_deg = 0
  r_ankle_joint_deg = 0
  r_hand_joint_deg = 0
  r_hip_joint_deg = 0
  r_p_sholder_joint_deg = 0
  r_r_sholder_joint_deg = 0
  r_r_wrist_joint_deg = 0
  r_shin_top_joint_deg = 0
  r_thigh_top_joint_deg = 0
  r_y_wrist_joint_deg = 0
  waist_joint_deg = 0
